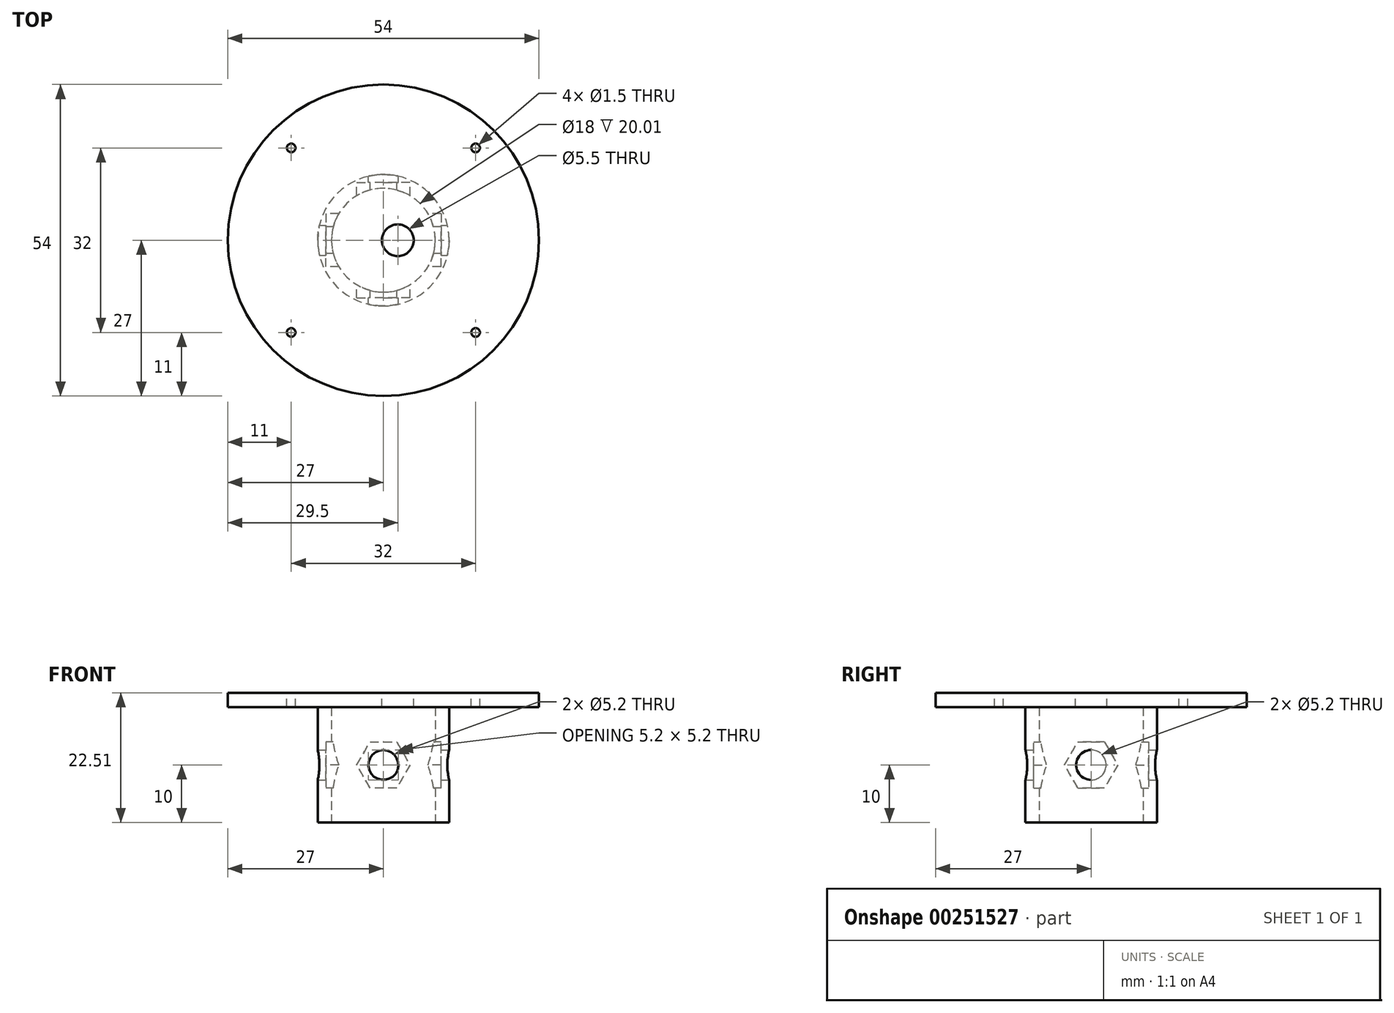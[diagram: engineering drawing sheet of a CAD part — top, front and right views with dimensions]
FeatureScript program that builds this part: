
annotation { "Feature Type Name" : "Feature", "Feature Type Description" : "" }
export const myFeature = defineFeature(function(context is Context, id is Id, definition is map)
    precondition{}
    {
        {
            var Q0;
            Q0=qCreatedBy(makeId("Top.planeOp"),FACE);
            var sketch = newSketch(context, id + "F0", { "sketchPlane" : qUnion([Q0])});
            skCircle(sketch, "E0", {"center": v(0, 0) * mm, "radius": 11.4 * mm});
            skPoint(sketch, "E1.0.midPoint", {"position": v(4.02, -6.97) * mm});
            skSolve(sketch);
        }
        {
            var Q0;
            Q0=makeQuery(id+"F0.imprint","IMPRINT",FACE,{"disambiguationData":[TD([[makeQuery(id+"F0.imprint","IMPRINT",EDGE,{"derivedFrom":sQuery(id+"F0.wireOp",EDGE,"E0")}),1.0]])]});
            extrude(context, id + "F1", {"entities" : qUnion([Q0]), "depth" : 0.01 * mm});
        }
        {
            var Q0;
            Q0=makeQuery(id+"F1.opExtrude","CAP_FACE",FACE,{"disambiguationData":[OSD([sQuery(id+"F0.wireOp",EDGE,"E0"),sQuery(id+"F0.wireOp",EDGE,"E1.0"),sQuery(id+"F0.wireOp",EDGE,"E1.1"),sQuery(id+"F0.wireOp",EDGE,"E1.2")])],"isStart":false});
            var sketch = newSketch(context, id + "F2", { "sketchPlane" : qUnion([Q0])});
            skCircle(sketch, "E2", {"center": v(0, 0) * mm, "radius": 9 * mm});
            skCircle(sketch, "E3", {"center": v(0, 0) * mm, "radius": 11.4 * mm});
            skSolve(sketch);
        }
        {
            var Q0;
            Q0=qSketchRegion(id+"F2",true);
            var Q1;
            Q1=makeQuery(id+"F2.imprint","IMPRINT",FACE,{"disambiguationData":[TD([[makeQuery(id+"F2.imprint","IMPRINT",EDGE,{"derivedFrom":sQuery(id+"F2.wireOp",EDGE,"E2")}),-1.0]])]});
            extrude(context, id + "F3", {"entities" : qUnion([Q0, Q1]), "operationType" : NewBodyOperationType.ADD, "depth" : 20 * mm});
        }
        {
            var Q0;
            Q0=qCreatedBy(makeId("Right.planeOp"),FACE);
            var sketch = newSketch(context, id + "F4", { "sketchPlane" : qUnion([Q0])});
            skLineSegment(sketch, "E4", {"start": v(0, 0) * mm, "end": v(0, 28.62) * mm, "construction": true});
            skCircle(sketch, "E5.cCircle", {"center": v(0, 10) * mm, "radius": 4 * mm, "construction": true});
            skLineSegment(sketch, "E5.0", {"start": v(2.3, 6) * mm, "end": v(-2.3, 6) * mm});
            skLineSegment(sketch, "E5.1", {"start": v(-2.3, 6) * mm, "end": v(-4.62, 10) * mm});
            skLineSegment(sketch, "E5.2", {"start": v(-4.62, 10) * mm, "end": v(-2.3, 14) * mm});
            skLineSegment(sketch, "E5.3", {"start": v(-2.3, 14) * mm, "end": v(2.3, 14) * mm});
            skLineSegment(sketch, "E5.4", {"start": v(2.3, 14) * mm, "end": v(4.62, 10) * mm});
            skLineSegment(sketch, "E5.5", {"start": v(4.62, 10) * mm, "end": v(2.3, 6) * mm});
            skPoint(sketch, "E5.0.midPoint", {"position": v(0, 6) * mm});
            skSolve(sketch);
        }
        {
            var Q0;
            Q0=qSketchRegion(id+"F4",true);
            extrude(context, id + "F5", {"entities" : qUnion([Q0]), "operationType" : NewBodyOperationType.REMOVE, "depth" : 10 * mm, "hasSecondDirection" : true, "secondDirectionOppositeDirection" : true, "secondDirectionDepth" : 10 * mm});
        }
        {
            var Q0;
            Q0=qCreatedBy(makeId("Front.planeOp"),FACE);
            var sketch = newSketch(context, id + "F6", { "sketchPlane" : qUnion([Q0])});
            skLineSegment(sketch, "E6", {"start": v(0, 0) * mm, "end": v(0, 40) * mm, "construction": true});
            skCircle(sketch, "E7.cCircle", {"center": v(0, 10) * mm, "radius": 4 * mm, "construction": true});
            skLineSegment(sketch, "E7.0", {"start": v(2.3, 6) * mm, "end": v(-2.3, 6) * mm});
            skLineSegment(sketch, "E7.1", {"start": v(-2.3, 6) * mm, "end": v(-4.62, 10) * mm});
            skLineSegment(sketch, "E7.2", {"start": v(-4.62, 10) * mm, "end": v(-2.3, 14) * mm});
            skLineSegment(sketch, "E7.3", {"start": v(-2.3, 14) * mm, "end": v(2.3, 14) * mm});
            skLineSegment(sketch, "E7.4", {"start": v(2.3, 14) * mm, "end": v(4.62, 10) * mm});
            skLineSegment(sketch, "E7.5", {"start": v(4.62, 10) * mm, "end": v(2.3, 6) * mm});
            skPoint(sketch, "E7.0.midPoint", {"position": v(0, 6) * mm});
            skSolve(sketch);
        }
        {
            var Q0;
            Q0=qSketchRegion(id+"F6",true);
            extrude(context, id + "F7", {"entities" : qUnion([Q0]), "operationType" : NewBodyOperationType.REMOVE, "depth" : 10 * mm, "hasSecondDirection" : true, "secondDirectionOppositeDirection" : true, "secondDirectionDepth" : 10 * mm});
        }
        {
            var Q0;
            Q0=qCreatedBy(makeId("Right.planeOp"),FACE);
            var sketch = newSketch(context, id + "F8", { "sketchPlane" : qUnion([Q0])});
            skLineSegment(sketch, "E8", {"start": v(0, 0) * mm, "end": v(0, 33.2) * mm});
            skCircle(sketch, "E9", {"center": v(0, 10) * mm, "radius": 2.6 * mm});
            skSolve(sketch);
        }
        {
            var Q0;
            Q0=qSketchRegion(id+"F8",true);
            extrude(context, id + "F9", {"entities" : qUnion([Q0]), "operationType" : NewBodyOperationType.REMOVE, "endBound" : BoundingType.THROUGH_ALL, "oppositeDirection" : true, "depth" : 25 * mm, "hasSecondDirection" : true, "secondDirectionBound" : SecondDirectionBoundingType.THROUGH_ALL, "secondDirectionOppositeDirection" : false, "secondDirectionDepth" : 25 * mm});
        }
        {
            var Q0;
            Q0=qCreatedBy(makeId("Front.planeOp"),FACE);
            var sketch = newSketch(context, id + "F10", { "sketchPlane" : qUnion([Q0])});
            skLineSegment(sketch, "E10", {"start": v(0, 0) * mm, "end": v(0, 19.64) * mm, "construction": true});
            skCircle(sketch, "E11", {"center": v(0, 10) * mm, "radius": 2.6 * mm});
            skSolve(sketch);
        }
        {
            var Q0;
            Q0=qSketchRegion(id+"F10",true);
            extrude(context, id + "F11", {"entities" : qUnion([Q0]), "operationType" : NewBodyOperationType.REMOVE, "endBound" : BoundingType.THROUGH_ALL, "depth" : 25 * mm, "hasSecondDirection" : true, "secondDirectionBound" : SecondDirectionBoundingType.THROUGH_ALL, "secondDirectionOppositeDirection" : true, "secondDirectionDepth" : 25 * mm});
        }
        {
            var Q0;
            Q0=makeQuery(id+"F1.opExtrude","CAP_FACE",FACE,{"disambiguationData":[OSD([sQuery(id+"F0.wireOp",EDGE,"E0")])],"isStart":false});
            var sketch = newSketch(context, id + "F12", { "sketchPlane" : qUnion([Q0])});
            skCircle(sketch, "E12", {"center": v(0, 0) * mm, "radius": 9 * mm});
            skSolve(sketch);
        }
        {
            var Q0;
            Q0 = qSketchRegion(id + "F12", true);
            extrude(context, id + "F13", {"entities" : qUnion([Q0]), "operationType" : NewBodyOperationType.REMOVE, "oppositeDirection" : true, "depth" : 10 * mm});
        }
        {
            var Q0;
            Q0=makeQuery(id+"F3.opExtrude","CAP_FACE",FACE,{"disambiguationData":[OSD([sQuery(id+"F2.wireOp",EDGE,"E2"),sQuery(id+"F2.wireOp",EDGE,"E3")])],"isStart":false});
            var sketch = newSketch(context, id + "F14", { "sketchPlane" : qUnion([Q0])});
            skCircle(sketch, "E13", {"center": v(0, 0) * mm, "radius": 27 * mm});
            skSolve(sketch);
        }
        {
            var Q0;
            Q0 = qSketchRegion(id + "F14", true);
            extrude(context, id + "F15", {"entities" : qUnion([Q0]), "operationType" : NewBodyOperationType.ADD, "depth" : 2.5 * mm});
        }
        {
            var Q0;
            Q0=makeQuery(id+"F15.opExtrude","CAP_FACE",FACE,{"disambiguationData":[OSD([sQuery(id+"F14.wireOp",EDGE,"E13")])],"isStart":false});
            var sketch = newSketch(context, id + "F16", { "sketchPlane" : qUnion([Q0])});
            skLineSegment(sketch, "E14", {"start": v(0, 0) * mm, "end": v(2.5, 0) * mm, "construction": true});
            skCircle(sketch, "E15", {"center": v(2.5, 0) * mm, "radius": 2.75 * mm});
            skSolve(sketch);
        }
        {
            var Q0;
            Q0 = qSketchRegion(id + "F16", true);
            extrude(context, id + "F17", {"entities" : qUnion([Q0]), "operationType" : NewBodyOperationType.REMOVE, "oppositeDirection" : true, "depth" : 25 * mm});
        }
        {
            var Q0;
            Q0=makeQuery(id+"F15.opExtrude","CAP_FACE",FACE,{"disambiguationData":[OSD([sQuery(id+"F14.wireOp",EDGE,"E13")])],"isStart":false});
            var sketch = newSketch(context, id + "F18", { "sketchPlane" : qUnion([Q0])});
            skLineSegment(sketch, "E16.bottom", {"start": v(-19, -19) * mm, "end": v(19, -19) * mm});
            skLineSegment(sketch, "E16.top", {"start": v(-19, 19) * mm, "end": v(19, 19) * mm});
            skLineSegment(sketch, "E16.left", {"start": v(-19, -19) * mm, "end": v(-19, 19) * mm});
            skLineSegment(sketch, "E16.right", {"start": v(19, -19) * mm, "end": v(19, 19) * mm});
            skPoint(sketch, "E16.middle", {"position": v(0, 0) * mm});
            skCircle(sketch, "E17", {"center": v(-16, 16) * mm, "radius": 0.75 * mm});
            skCircle(sketch, "E18", {"center": v(16, 16) * mm, "radius": 0.75 * mm});
            skCircle(sketch, "E19", {"center": v(16, -16) * mm, "radius": 0.75 * mm});
            skCircle(sketch, "E20", {"center": v(-16, -16) * mm, "radius": 0.75 * mm});
            skSolve(sketch);
        }
        {
            var Q0;
            Q0=makeQuery(id+"F18.imprint","IMPRINT",FACE,{"disambiguationData":[TD([[makeQuery(id+"F18.imprint","IMPRINT",EDGE,{"derivedFrom":sQuery(id+"F18.wireOp",EDGE,"E20")}),1.0]])]});
            var Q1;
            Q1=makeQuery(id+"F18.imprint","IMPRINT",FACE,{"disambiguationData":[TD([[makeQuery(id+"F18.imprint","IMPRINT",EDGE,{"derivedFrom":sQuery(id+"F18.wireOp",EDGE,"E19")}),1.0]])]});
            var Q2;
            Q2=makeQuery(id+"F18.imprint","IMPRINT",FACE,{"disambiguationData":[TD([[makeQuery(id+"F18.imprint","IMPRINT",EDGE,{"derivedFrom":sQuery(id+"F18.wireOp",EDGE,"E17")}),1.0]])]});
            var Q3;
            Q3=makeQuery(id+"F18.imprint","IMPRINT",FACE,{"disambiguationData":[TD([[makeQuery(id+"F18.imprint","IMPRINT",EDGE,{"derivedFrom":sQuery(id+"F18.wireOp",EDGE,"E18")}),1.0]])]});
            extrude(context, id + "F19", {"entities" : qUnion([Q0, Q1, Q2, Q3]), "operationType" : NewBodyOperationType.REMOVE, "oppositeDirection" : true, "depth" : 25 * mm});
        }
    });
